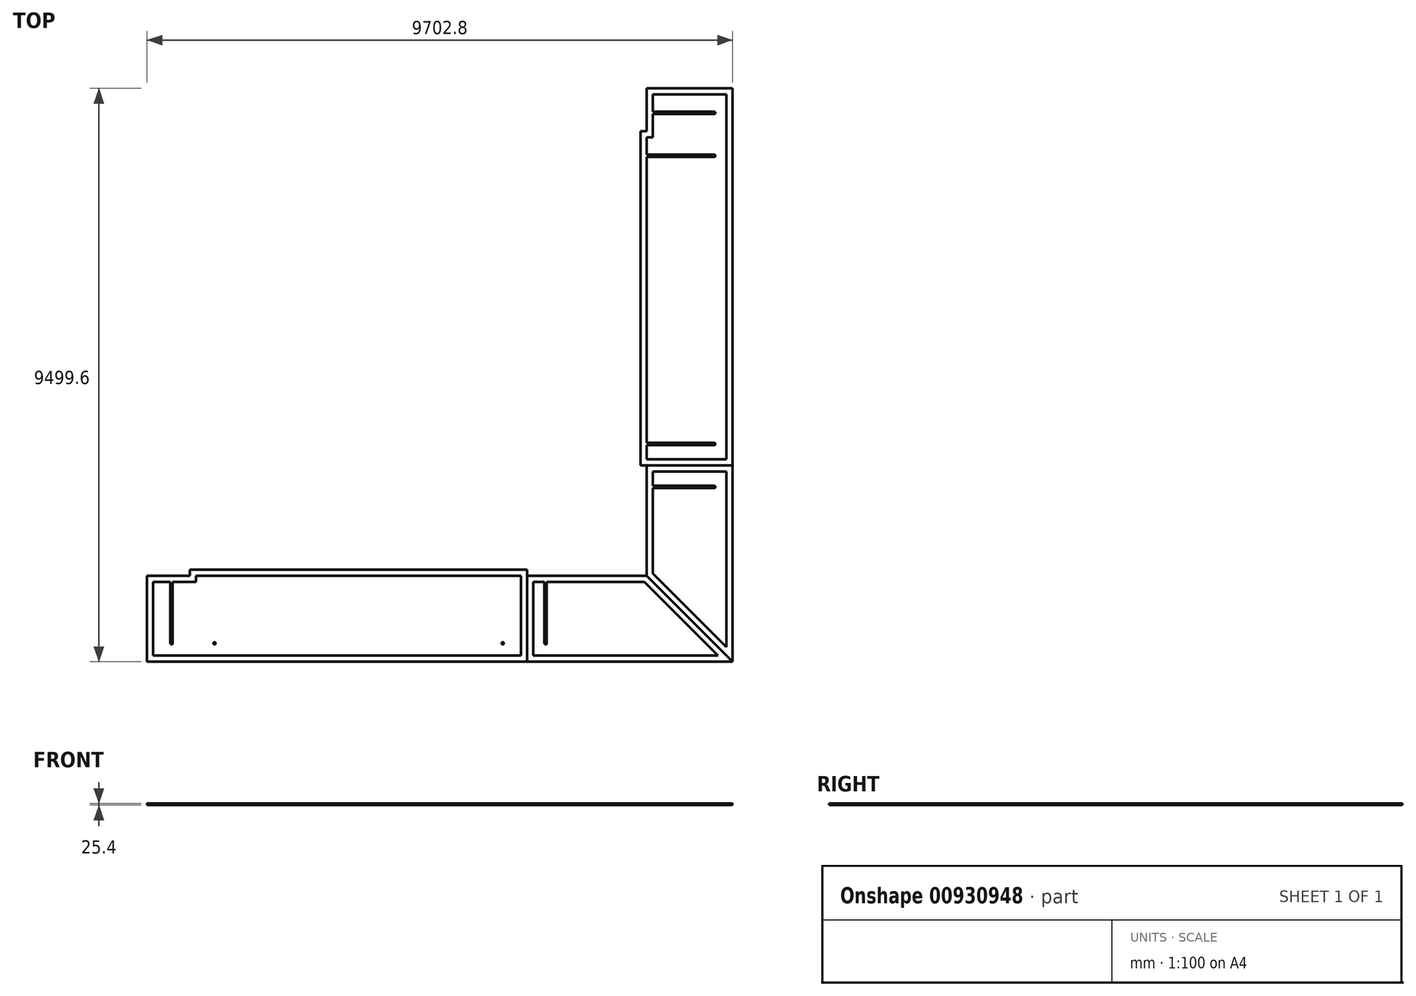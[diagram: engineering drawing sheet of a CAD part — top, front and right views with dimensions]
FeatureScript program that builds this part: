
annotation { "Feature Type Name" : "Feature", "Feature Type Description" : "" }
export const myFeature = defineFeature(function(context is Context, id is Id, definition is map)
    precondition{}
    {
        {
            var Q0;
            Q0=qCreatedBy(makeId("Top.planeOp"),FACE);
            var sketch = newSketch(context, id + "F0", { "sketchPlane" : qUnion([Q0])});
            skLineSegment(sketch, "E0.top", {"start": v(0, -1422.4) * mm, "end": v(9702.8, -1422.4) * mm});
            skLineSegment(sketch, "E0.left", {"start": v(0, 0) * mm, "end": v(0, -1422.4) * mm});
            skLineSegment(sketch, "E1.top", {"start": v(101.6, -1320.8) * mm, "end": v(6197.6, -1320.8) * mm});
            skLineSegment(sketch, "E1.left", {"start": v(101.6, -101.6) * mm, "end": v(101.6, -1320.8) * mm});
            skLineSegment(sketch, "E2.bottom", {"start": v(387.35, -101.6) * mm, "end": v(425.45, -101.6) * mm});
            skLineSegment(sketch, "E2.top", {"start": v(387.35, -1117.6) * mm, "end": v(425.45, -1117.6) * mm});
            skLineSegment(sketch, "E2.left", {"start": v(387.35, -101.6) * mm, "end": v(387.35, -1117.6) * mm});
            skLineSegment(sketch, "E2.right", {"start": v(425.45, -101.6) * mm, "end": v(425.45, -1117.6) * mm});
            skLineSegment(sketch, "E3.bottom", {"start": v(6584.95, -101.6) * mm, "end": v(6623.05, -101.6) * mm});
            skLineSegment(sketch, "E3.top", {"start": v(6584.95, -1117.6) * mm, "end": v(6623.05, -1117.6) * mm});
            skLineSegment(sketch, "E3.left", {"start": v(6584.95, -101.6) * mm, "end": v(6584.95, -1117.6) * mm});
            skLineSegment(sketch, "E3.right", {"start": v(6623.05, -101.6) * mm, "end": v(6623.05, -1117.6) * mm});
            skCircle(sketch, "E4", {"center": v(406.4, -1117.6) * mm, "radius": 19.05 * mm});
            skCircle(sketch, "E5", {"center": v(6604, -1117.6) * mm, "radius": 19.05 * mm});
            skLineSegment(sketch, "E6", {"start": v(101.6, -101.6) * mm, "end": v(812.8, -101.6) * mm});
            skLineSegment(sketch, "E7", {"start": v(812.8, -101.6) * mm, "end": v(812.8, 0) * mm});
            skLineSegment(sketch, "E8", {"start": v(812.8, 0) * mm, "end": v(6197.6, 0) * mm});
            skLineSegment(sketch, "E9", {"start": v(6197.6, 0) * mm, "end": v(6197.6, -101.6) * mm});
            skLineSegment(sketch, "E10", {"start": v(6400.8, -101.6) * mm, "end": v(8238.32, -101.6) * mm});
            skLineSegment(sketch, "E11", {"start": v(0, 0) * mm, "end": v(711.2, 0) * mm});
            skLineSegment(sketch, "E12", {"start": v(711.2, 0) * mm, "end": v(711.2, 101.6) * mm});
            skLineSegment(sketch, "E13", {"start": v(711.2, 101.6) * mm, "end": v(6299.2, 101.6) * mm});
            skLineSegment(sketch, "E14", {"start": v(6299.2, 101.6) * mm, "end": v(6299.2, 0) * mm});
            skLineSegment(sketch, "E15", {"start": v(6299.2, 0) * mm, "end": v(8280.4, 0) * mm});
            skLineSegment(sketch, "E16.bottom", {"start": v(1098.55, 0) * mm, "end": v(1136.65, 0) * mm});
            skLineSegment(sketch, "E16.top", {"start": v(1098.55, -1117.6) * mm, "end": v(1136.65, -1117.6) * mm});
            skLineSegment(sketch, "E16.left", {"start": v(1098.55, 0) * mm, "end": v(1098.55, -1117.6) * mm});
            skLineSegment(sketch, "E16.right", {"start": v(1136.65, 0) * mm, "end": v(1136.65, -1117.6) * mm});
            skLineSegment(sketch, "E17.bottom", {"start": v(5873.75, 0) * mm, "end": v(5911.85, 0) * mm});
            skLineSegment(sketch, "E17.top", {"start": v(5873.75, -1117.6) * mm, "end": v(5911.85, -1117.6) * mm});
            skLineSegment(sketch, "E17.left", {"start": v(5873.75, 0) * mm, "end": v(5873.75, -1117.6) * mm});
            skLineSegment(sketch, "E17.right", {"start": v(5911.85, 0) * mm, "end": v(5911.85, -1117.6) * mm});
            skCircle(sketch, "E18", {"center": v(1117.6, -1117.6) * mm, "radius": 19.05 * mm});
            skCircle(sketch, "E19", {"center": v(5892.8, -1117.6) * mm, "radius": 19.05 * mm});
            skLineSegment(sketch, "E20", {"start": v(8280.4, 0) * mm, "end": v(8280.4, 1828.8) * mm});
            skLineSegment(sketch, "E21", {"start": v(8178.8, 1828.8) * mm, "end": v(8280.4, 1828.8) * mm});
            skLineSegment(sketch, "E22", {"start": v(8178.8, 1828.8) * mm, "end": v(8178.8, 7366) * mm});
            skLineSegment(sketch, "E23", {"start": v(8178.8, 7366) * mm, "end": v(8280.4, 7366) * mm});
            skLineSegment(sketch, "E24", {"start": v(8280.4, 7366) * mm, "end": v(8280.4, 8077.2) * mm});
            skLineSegment(sketch, "E25", {"start": v(8280.4, 8077.2) * mm, "end": v(9702.8, 8077.2) * mm});
            skLineSegment(sketch, "E26", {"start": v(9702.8, 8077.2) * mm, "end": v(9702.8, -1422.4) * mm});
            skLineSegment(sketch, "E27", {"start": v(8382, 42.08) * mm, "end": v(8382, 1727.2) * mm});
            skLineSegment(sketch, "E28", {"start": v(8382, 1930.4) * mm, "end": v(8280.4, 1930.4) * mm});
            skLineSegment(sketch, "E29", {"start": v(8280.4, 1930.4) * mm, "end": v(8280.4, 7264.4) * mm});
            skLineSegment(sketch, "E30", {"start": v(8280.4, 7264.4) * mm, "end": v(8382, 7264.4) * mm});
            skLineSegment(sketch, "E31", {"start": v(8382, 7264.4) * mm, "end": v(8382, 7975.6) * mm});
            skLineSegment(sketch, "E32", {"start": v(8382, 7975.6) * mm, "end": v(9601.2, 7975.6) * mm});
            skLineSegment(sketch, "E33", {"start": v(9601.2, 7975.6) * mm, "end": v(9601.2, 1930.4) * mm});
            skLineSegment(sketch, "E34.bottom", {"start": v(8382, 1492.25) * mm, "end": v(9398, 1492.25) * mm});
            skLineSegment(sketch, "E34.top", {"start": v(8382, 1454.15) * mm, "end": v(9398, 1454.15) * mm});
            skLineSegment(sketch, "E34.left", {"start": v(8382, 1492.25) * mm, "end": v(8382, 1454.15) * mm});
            skLineSegment(sketch, "E34.right", {"start": v(9398, 1492.25) * mm, "end": v(9398, 1454.15) * mm});
            skLineSegment(sketch, "E35.bottom", {"start": v(8280.4, 2203.45) * mm, "end": v(9398, 2203.45) * mm});
            skLineSegment(sketch, "E35.top", {"start": v(8280.4, 2165.35) * mm, "end": v(9398, 2165.35) * mm});
            skLineSegment(sketch, "E35.left", {"start": v(8280.4, 2203.45) * mm, "end": v(8280.4, 2165.35) * mm});
            skLineSegment(sketch, "E35.right", {"start": v(9398, 2203.45) * mm, "end": v(9398, 2165.35) * mm});
            skLineSegment(sketch, "E36.bottom", {"start": v(8280.4, 6978.65) * mm, "end": v(9398, 6978.65) * mm});
            skLineSegment(sketch, "E36.top", {"start": v(8280.4, 6940.55) * mm, "end": v(9398, 6940.55) * mm});
            skLineSegment(sketch, "E36.left", {"start": v(8280.4, 6978.65) * mm, "end": v(8280.4, 6940.55) * mm});
            skLineSegment(sketch, "E36.right", {"start": v(9398, 6978.65) * mm, "end": v(9398, 6940.55) * mm});
            skLineSegment(sketch, "E37.bottom", {"start": v(8382, 7689.85) * mm, "end": v(9398, 7689.85) * mm});
            skLineSegment(sketch, "E37.top", {"start": v(8382, 7651.75) * mm, "end": v(9398, 7651.75) * mm});
            skLineSegment(sketch, "E37.left", {"start": v(8382, 7689.85) * mm, "end": v(8382, 7651.75) * mm});
            skLineSegment(sketch, "E37.right", {"start": v(9398, 7689.85) * mm, "end": v(9398, 7651.75) * mm});
            skCircle(sketch, "E38", {"center": v(9398, 7670.8) * mm, "radius": 19.05 * mm});
            skCircle(sketch, "E39", {"center": v(9398, 6959.6) * mm, "radius": 19.05 * mm});
            skCircle(sketch, "E40", {"center": v(9398, 2184.4) * mm, "radius": 19.05 * mm});
            skCircle(sketch, "E41", {"center": v(9398, 1473.2) * mm, "radius": 19.05 * mm});
            skLineSegment(sketch, "E42.left", {"start": v(6197.6, -101.6) * mm, "end": v(6197.6, -1320.8) * mm});
            skLineSegment(sketch, "E42.right", {"start": v(6299.2, -101.6) * mm, "end": v(6299.2, -1422.4) * mm});
            skLineSegment(sketch, "E43.bottom", {"start": v(6299.2, 0) * mm, "end": v(6400.8, 0) * mm});
            skLineSegment(sketch, "E43.left", {"start": v(6299.2, 0) * mm, "end": v(6299.2, -1320.8) * mm});
            skLineSegment(sketch, "E43.right", {"start": v(6400.8, -101.6) * mm, "end": v(6400.8, -1320.8) * mm});
            skLineSegment(sketch, "E44.trimOffspring", {"start": v(6400.8, -1320.8) * mm, "end": v(9457.52, -1320.8) * mm});
            skLineSegment(sketch, "E45", {"start": v(8382, 1930.4) * mm, "end": v(9601.2, 1930.4) * mm});
            skLineSegment(sketch, "E46", {"start": v(8382, 1828.8) * mm, "end": v(9702.8, 1828.8) * mm});
            skLineSegment(sketch, "E47", {"start": v(8382, 1727.2) * mm, "end": v(9601.2, 1727.2) * mm});
            skLineSegment(sketch, "E48.trimOffspring", {"start": v(9601.2, 1727.2) * mm, "end": v(9601.2, -1177.12) * mm});
            skLineSegment(sketch, "E49", {"start": v(8382, 1828.8) * mm, "end": v(8280.4, 1828.8) * mm});
            skLineSegment(sketch, "E50", {"start": v(8280.4, 0) * mm, "end": v(9702.8, -1422.4) * mm});
            skLineSegment(sketch, "E51", {"start": v(8238.32, -101.6) * mm, "end": v(9457.52, -1320.8) * mm});
            skLineSegment(sketch, "E52", {"start": v(8382, 42.08) * mm, "end": v(9601.2, -1177.12) * mm});
            skSolve(sketch);
        }
        {
            var Q0;
            {var subQ11=sQuery(id+"F0.wireOp",EDGE,"E0.left");Q0=makeQuery(id+"F0.imprint","IMPRINT",FACE,{"disambiguationData":[TD([[makeQuery(id+"F0.imprint","IMPRINT",EDGE,{"derivedFrom":subQ11}),1.0]])]});}
            var Q1;
            {var subQ0=sQuery(id+"F0.wireOp",EDGE,"E2.left");Q1=makeQuery(id+"F0.imprint","IMPRINT",FACE,{"disambiguationData":[TD([[makeQuery(id+"F0.imprint","IMPRINT",EDGE,{"derivedFrom":subQ0}),1.0]])]});}
            var Q2;
            {var subQ0=sQuery(id+"F0.wireOp",EDGE,"E2.top");Q2=makeQuery(id+"F0.imprint","IMPRINT",FACE,{"disambiguationData":[TD([[makeQuery(id+"F0.imprint","IMPRINT",EDGE,{"derivedFrom":subQ0}),1.0]])]});}
            var Q3;
            {var subQ0=sQuery(id+"F0.wireOp",EDGE,"E2.top");Q3=makeQuery(id+"F0.imprint","IMPRINT",FACE,{"disambiguationData":[TD([[makeQuery(id+"F0.imprint","IMPRINT",EDGE,{"derivedFrom":subQ0}),-1.0]])]});}
            var Q4;
            Q4=makeQuery(id+"F0.imprint","IMPRINT",FACE,{"disambiguationData":[TD([[makeQuery(id+"F0.imprint","IMPRINT",EDGE,{"derivedFrom":sQuery(id+"F0.wireOp",EDGE,"E16.bottom")}),-1.0]])]});
            var Q5;
            {var subQ0=sQuery(id+"F0.wireOp",EDGE,"E16.top");Q5=makeQuery(id+"F0.imprint","IMPRINT",FACE,{"disambiguationData":[TD([[makeQuery(id+"F0.imprint","IMPRINT",EDGE,{"derivedFrom":subQ0}),1.0]])]});}
            var Q6;
            {var subQ0=sQuery(id+"F0.wireOp",EDGE,"E16.top");Q6=makeQuery(id+"F0.imprint","IMPRINT",FACE,{"disambiguationData":[TD([[makeQuery(id+"F0.imprint","IMPRINT",EDGE,{"derivedFrom":subQ0}),-1.0]])]});}
            var Q7;
            Q7=makeQuery(id+"F0.imprint","IMPRINT",FACE,{"disambiguationData":[TD([[makeQuery(id+"F0.imprint","IMPRINT",EDGE,{"derivedFrom":sQuery(id+"F0.wireOp",EDGE,"E17.bottom")}),-1.0]])]});
            var Q8;
            {var subQ0=sQuery(id+"F0.wireOp",EDGE,"E17.top");Q8=makeQuery(id+"F0.imprint","IMPRINT",FACE,{"disambiguationData":[TD([[makeQuery(id+"F0.imprint","IMPRINT",EDGE,{"derivedFrom":subQ0}),1.0]])]});}
            var Q9;
            {var subQ0=sQuery(id+"F0.wireOp",EDGE,"E17.top");Q9=makeQuery(id+"F0.imprint","IMPRINT",FACE,{"disambiguationData":[TD([[makeQuery(id+"F0.imprint","IMPRINT",EDGE,{"derivedFrom":subQ0}),-1.0]])]});}
            extrude(context, id + "F1", {"entities" : qUnion([Q0, Q1, Q2, Q3, Q4, Q5, Q6, Q7, Q8, Q9]), "depth" : 25.4 * mm, "offsetDistance" : 25.4 * mm});
        }
        {
            var Q0;
            Q0=makeQuery(id+"F0.imprint","IMPRINT",FACE,{"disambiguationData":[TD([[makeQuery(id+"F0.imprint","IMPRINT",EDGE,{"derivedFrom":sQuery(id+"F0.wireOp",EDGE,"E15")}),-1.0]])]});
            var Q1;
            {var subQ0=sQuery(id+"F0.wireOp",EDGE,"E3.left");Q1=makeQuery(id+"F0.imprint","IMPRINT",FACE,{"disambiguationData":[TD([[makeQuery(id+"F0.imprint","IMPRINT",EDGE,{"derivedFrom":subQ0}),1.0]])]});}
            var Q2;
            {var subQ0=sQuery(id+"F0.wireOp",EDGE,"E3.top");Q2=makeQuery(id+"F0.imprint","IMPRINT",FACE,{"disambiguationData":[TD([[makeQuery(id+"F0.imprint","IMPRINT",EDGE,{"derivedFrom":subQ0}),1.0]])]});}
            var Q3;
            {var subQ0=sQuery(id+"F0.wireOp",EDGE,"E3.top");Q3=makeQuery(id+"F0.imprint","IMPRINT",FACE,{"disambiguationData":[TD([[makeQuery(id+"F0.imprint","IMPRINT",EDGE,{"derivedFrom":subQ0}),-1.0]])]});}
            extrude(context, id + "F2", {"entities" : qUnion([Q0, Q1, Q2, Q3]), "depth" : 25.4 * mm, "offsetDistance" : 25.4 * mm});
        }
        {
            var Q0;
            Q0=makeQuery(id+"F0.imprint","IMPRINT",FACE,{"disambiguationData":[TD([[makeQuery(id+"F0.imprint","IMPRINT",EDGE,{"derivedFrom":sQuery(id+"F0.wireOp",EDGE,"E20")}),-1.0]])]});
            var Q1;
            {var subQ0=sQuery(id+"F0.wireOp",EDGE,"E34.bottom");Q1=makeQuery(id+"F0.imprint","IMPRINT",FACE,{"disambiguationData":[TD([[makeQuery(id+"F0.imprint","IMPRINT",EDGE,{"derivedFrom":subQ0}),-1.0]])]});}
            var Q2;
            {var subQ0=sQuery(id+"F0.wireOp",EDGE,"E34.right");Q2=makeQuery(id+"F0.imprint","IMPRINT",FACE,{"disambiguationData":[TD([[makeQuery(id+"F0.imprint","IMPRINT",EDGE,{"derivedFrom":subQ0}),-1.0]])]});}
            var Q3;
            {var subQ0=sQuery(id+"F0.wireOp",EDGE,"E34.right");Q3=makeQuery(id+"F0.imprint","IMPRINT",FACE,{"disambiguationData":[TD([[makeQuery(id+"F0.imprint","IMPRINT",EDGE,{"derivedFrom":subQ0}),1.0]])]});}
            extrude(context, id + "F3", {"entities" : qUnion([Q0, Q1, Q2, Q3]), "depth" : 25.4 * mm, "offsetDistance" : 25.4 * mm});
        }
        {
            var Q0;
            Q0=makeQuery(id+"F0.imprint","IMPRINT",FACE,{"disambiguationData":[TD([[makeQuery(id+"F0.imprint","IMPRINT",EDGE,{"derivedFrom":sQuery(id+"F0.wireOp",EDGE,"E21")}),1.0]])]});
            var Q1;
            {var subQ0=sQuery(id+"F0.wireOp",EDGE,"E35.bottom");Q1=makeQuery(id+"F0.imprint","IMPRINT",FACE,{"disambiguationData":[TD([[makeQuery(id+"F0.imprint","IMPRINT",EDGE,{"derivedFrom":subQ0}),-1.0]])]});}
            var Q2;
            {var subQ0=sQuery(id+"F0.wireOp",EDGE,"E35.right");Q2=makeQuery(id+"F0.imprint","IMPRINT",FACE,{"disambiguationData":[TD([[makeQuery(id+"F0.imprint","IMPRINT",EDGE,{"derivedFrom":subQ0}),-1.0]])]});}
            var Q3;
            {var subQ0=sQuery(id+"F0.wireOp",EDGE,"E35.right");Q3=makeQuery(id+"F0.imprint","IMPRINT",FACE,{"disambiguationData":[TD([[makeQuery(id+"F0.imprint","IMPRINT",EDGE,{"derivedFrom":subQ0}),1.0]])]});}
            var Q4;
            {var subQ0=sQuery(id+"F0.wireOp",EDGE,"E36.bottom");Q4=makeQuery(id+"F0.imprint","IMPRINT",FACE,{"disambiguationData":[TD([[makeQuery(id+"F0.imprint","IMPRINT",EDGE,{"derivedFrom":subQ0}),-1.0]])]});}
            var Q5;
            {var subQ0=sQuery(id+"F0.wireOp",EDGE,"E36.right");Q5=makeQuery(id+"F0.imprint","IMPRINT",FACE,{"disambiguationData":[TD([[makeQuery(id+"F0.imprint","IMPRINT",EDGE,{"derivedFrom":subQ0}),-1.0]])]});}
            var Q6;
            {var subQ0=sQuery(id+"F0.wireOp",EDGE,"E36.right");Q6=makeQuery(id+"F0.imprint","IMPRINT",FACE,{"disambiguationData":[TD([[makeQuery(id+"F0.imprint","IMPRINT",EDGE,{"derivedFrom":subQ0}),1.0]])]});}
            var Q7;
            {var subQ0=sQuery(id+"F0.wireOp",EDGE,"E37.bottom");Q7=makeQuery(id+"F0.imprint","IMPRINT",FACE,{"disambiguationData":[TD([[makeQuery(id+"F0.imprint","IMPRINT",EDGE,{"derivedFrom":subQ0}),-1.0]])]});}
            var Q8;
            {var subQ0=sQuery(id+"F0.wireOp",EDGE,"E37.right");Q8=makeQuery(id+"F0.imprint","IMPRINT",FACE,{"disambiguationData":[TD([[makeQuery(id+"F0.imprint","IMPRINT",EDGE,{"derivedFrom":subQ0}),-1.0]])]});}
            var Q9;
            {var subQ0=sQuery(id+"F0.wireOp",EDGE,"E37.right");Q9=makeQuery(id+"F0.imprint","IMPRINT",FACE,{"disambiguationData":[TD([[makeQuery(id+"F0.imprint","IMPRINT",EDGE,{"derivedFrom":subQ0}),1.0]])]});}
            extrude(context, id + "F4", {"entities" : qUnion([Q0, Q1, Q2, Q3, Q4, Q5, Q6, Q7, Q8, Q9]), "depth" : 25.4 * mm, "offsetDistance" : 25.4 * mm});
        }
    });
